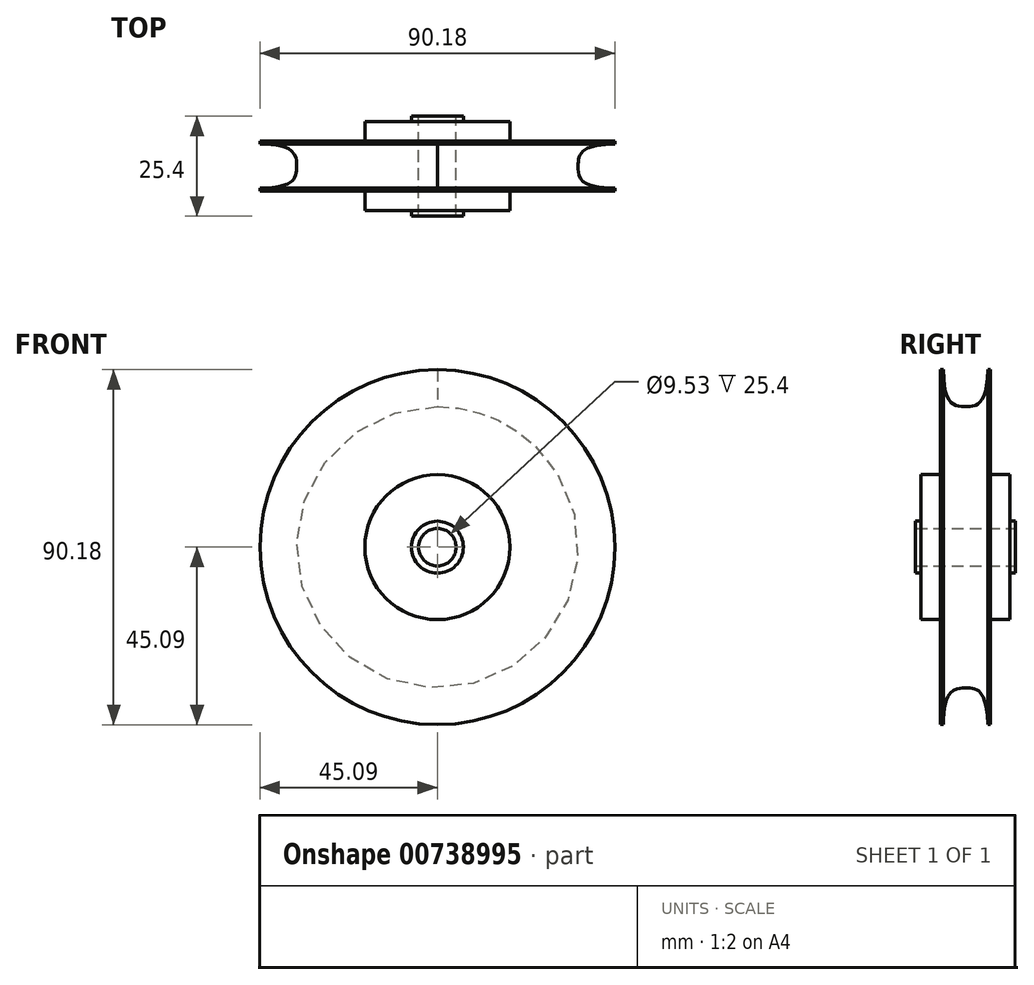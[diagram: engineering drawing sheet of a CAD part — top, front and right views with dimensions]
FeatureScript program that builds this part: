
annotation { "Feature Type Name" : "Feature", "Feature Type Description" : "" }
export const myFeature = defineFeature(function(context is Context, id is Id, definition is map)
    precondition{}
    {
        {
            var Q0;
            Q0=qCreatedBy(makeId("Front.planeOp"),FACE);
            var sketch = newSketch(context, id + "F0", { "sketchPlane" : qUnion([Q0])});
            skCircle(sketch, "E0", {"center": v(0, 0) * mm, "radius": 4.76 * mm});
            skCircle(sketch, "E1", {"center": v(0, 0) * mm, "radius": 45.09 * mm});
            skCircle(sketch, "E2", {"center": v(0, 0) * mm, "radius": 18.41 * mm});
            skCircle(sketch, "E3", {"center": v(0, 0) * mm, "radius": 6.6 * mm});
            skSolve(sketch);
        }
        {
            var Q0;
            Q0 = qSketchRegion(id + "F0", true);
            extrude(context, id + "F1", {"entities" : qUnion([Q0]), "endBound" : BoundingType.SYMMETRIC, "depth" : 12.7 * mm, "offsetDistance" : 25.4 * mm});
        }
        {
            var Q0;
            Q0=makeQuery(id+"F0.imprint","IMPRINT",FACE,{"disambiguationData":[TD([[makeQuery(id+"F0.imprint","IMPRINT",EDGE,{"derivedFrom":sQuery(id+"F0.wireOp",EDGE,"E2")}),1.0]])]});
            extrude(context, id + "F2", {"entities" : qUnion([Q0]), "operationType" : NewBodyOperationType.ADD, "endBound" : BoundingType.SYMMETRIC, "depth" : 22.6 * mm, "offsetDistance" : 25.4 * mm});
        }
        {
            var Q0;
            Q0=makeQuery(id+"F0.imprint","IMPRINT",FACE,{"disambiguationData":[TD([[makeQuery(id+"F0.imprint","IMPRINT",EDGE,{"derivedFrom":sQuery(id+"F0.wireOp",EDGE,"E0")}),-1.0]])]});
            extrude(context, id + "F3", {"entities" : qUnion([Q0]), "operationType" : NewBodyOperationType.ADD, "endBound" : BoundingType.SYMMETRIC, "depth" : 25.4 * mm, "offsetDistance" : 25.4 * mm});
        }
        {
            var Q0;
            Q0=qCreatedBy(makeId("Right.planeOp"),FACE);
            var sketch = newSketch(context, id + "F4", { "sketchPlane" : qUnion([Q0])});
            skFitSpline(sketch, "E4", {"points": [v(-5.57, 45.29) * mm, v(0, 35.76) * mm, v(5.66, 45.29) * mm], "startDerivative": vector(0, -56.47) * mm, "endDerivative": vector(0.31, 56.4) * mm});
            skLineSegment(sketch, "E5", {"start": v(-5.57, 45.29) * mm, "end": v(5.66, 45.29) * mm});
            skSolve(sketch);
        }
        {
            var Q0;
            Q0 = qSketchRegion(id + "F4", true);
            var Q1;
            Q1=sQuery(id+"F0.wireOp",EDGE,"E1");
            revolve(context, id + "F5", {"operationType" : NewBodyOperationType.REMOVE, "surfaceOperationType" : NewSurfaceOperationType.NEW, "entities" : qUnion([Q0]), "axis" : qUnion([Q1]), "revolveType" : RevolveType.FULL});
        }
    });
